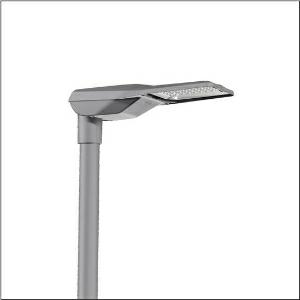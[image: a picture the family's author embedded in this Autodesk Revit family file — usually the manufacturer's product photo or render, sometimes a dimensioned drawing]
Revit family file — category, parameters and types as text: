
# Revit family: streetlight_sl_21_iq_mini___p0_5a_5xe2v31g08gb_39a9
name_source: partatom
category: Lighting Fixtures
units: mm (PartAtom-declared; Revit-internal decimal feet)

## family parameters
Cut with Voids When Loaded = No
Host = Face
Light Source = No
Part Type = Normal
Room Calculation Point = No
Round Connector Dimension = Use Diameter
Shared = No

## types (1)
- --- (1 x LED, 5580 lm, 37.1 W, 3000K)
    Apparent Load = 37 VA
    CIE Flux Codes = 37 73 96 100 100
    Color Rendering = 70
    Color Temperature = 3000K
    Default Elevation = 1800 mm
    Description = Streetlight SL 21 iQ mini, mast luminaire, primary light control with lens, of PMMA, primary optical cover: cover, of toughened safety glass, transparent, light distribution: P0.5a, light emission: direct distribution, primary light characteristic: asymmetric, installation type: post-top, side-entry, LED, High Power LED, rated luminous flux: 5.580lm, luminous efficacy: 150lm/W, light colour: 730, colour temperature: 3000K, control gear: iQ Street-Remote, control: pre-setting: linear dimming characteristic, Street-Remote, Auto-Match, Temp-Guard, Lumen-Switch, Night-Set, Smart-Wire, Light-Fading, Desk-Remote (wireless, voltage-free reading and setting of iQ features in the workshop via application-optimized NFC function/RFID function), optimised constant luminous flux control (CLO 2.0), mains connection: 220..240V, AC, 50/60Hz, start of lifetime: 37W, end of service life: 39W, reduction: 18W, luminaire housing, of diecast aluminium, powder-coated, Siteco® metallic grey (DB 702S), corrosivity category C5 mid according to DIN EN ISO 12944, please order mast flange separately, inclination adjustable: 0°, 5°, 10°, 15°, sealing non-destructively replaceable, multi-level sealing system, length: 628mm, width: 235mm, height: 110mm, mast flange for spigot size: 42mm (side-entry): 5XC10008XM4, 60/48mm (side-entry/post-top): 5XC10108XM2, 76/60mm (side-entry/post-top): 5XC10108XM1, mounting height: 4..8m, protection rating (complete): IP66, insulation class (complete): insulation class II (safety insulation), certification: CE, ENEC, ENEC+, VDE, impact resistance: IK10, permissible operating ambient temperature for outdoor applications: -40..+50°C, standard-compliant lighting for roads and squares, packaging unit: 1 piece

Light Distribution: P0.5a
    Height = 110 mm
    Lamp = 1 x LED
    Lamp Light Flux = 5580 lm
    Lamp Power = 37.1 W
    Lamp count = 1
    Length = 625 mm
    Luminous efficacy = 150 lm/W
    Manufacturer = Siteco
    ModVariant = No
    Model = 5XE2V31G08GB
    Number of Poles = 1
    OnlyDefault = Yes
    Power Factor = 1
    Product Name = Streetlight SL 21 iQ mini | P0.5a
    Product group = mast luminaire | pylon top
    ProductGroupID = 6100
    Protection Class = Protection class II
    Protection Degree = IP 66
    RLX_Detail_Level = 1
    RLX_Emergency_Light_Flux = 0 lm
    RLX_Emergency_Type = 0
    RLX_Emergency_Type_DB = No
    RlxData = <blob elided: 25861 chars, md5=e4cb07c9>
    Socket = socket
    Standby Power = 0 W
    System Light Flux = 5580 lm
    System Power = 37 W
    Type Comments = factory setting: luminous flux: 100 % | dim-lin: 254 | 385 mA
    Type Image = l_1003519.jpg
    URL = http://relux.com
    VarID = @adj_069990
    Voltage = 0 V
    Weight = 0.00 kg
    Width = 234 mm

## geometry (parser evidence)
native form markers: Blend x4, Sweep x10
no freeform markers — native parametric forms only
